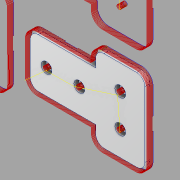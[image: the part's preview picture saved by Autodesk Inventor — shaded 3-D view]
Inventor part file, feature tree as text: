
AUTODESK INVENTOR PART (.ipt)
format: ipt  version: 2021.3 (Build 253353000, 353)  size: 199,680 bytes
history: native  units: in
note: dims shown in document units (in); Inventor stores cm internally (conversion verified against a paired STEP export)
features: other x10, reference x7, extrude x1, fillet x1
ambient origin geometry x8: Origin, YZ Plane, XZ Plane, XY Plane, X Axis, Y Axis, Z Axis, Center Point
bodies: Body1 (feature_tree)
feature tree (19):
  other  "wheel_frame_mount"
  other  "ソリッド1"
  other  "作業平面1"
  extrude  "押し出し1"  Depth=1.5748in
  fillet  "フィレット1"  Radius=1.1811in
  reference  "参照5"
  reference  "参照6"
  reference  "参照7"
  reference  "参照8"
  reference  "参照9"
  reference  "参照10"
  reference  "参照11"
  other  "<userpath>\workspace\beetle_inventor_model\suspension\bogie.iam"
  other  "bogie.iam"
  other  "wheel_with_mounts:2"
  other  "wheel_mount:2"
  other  "wheel_mount"
  other  "AFS-2040-4-130:1"
  other  "AFS-2040-4-50:1"
